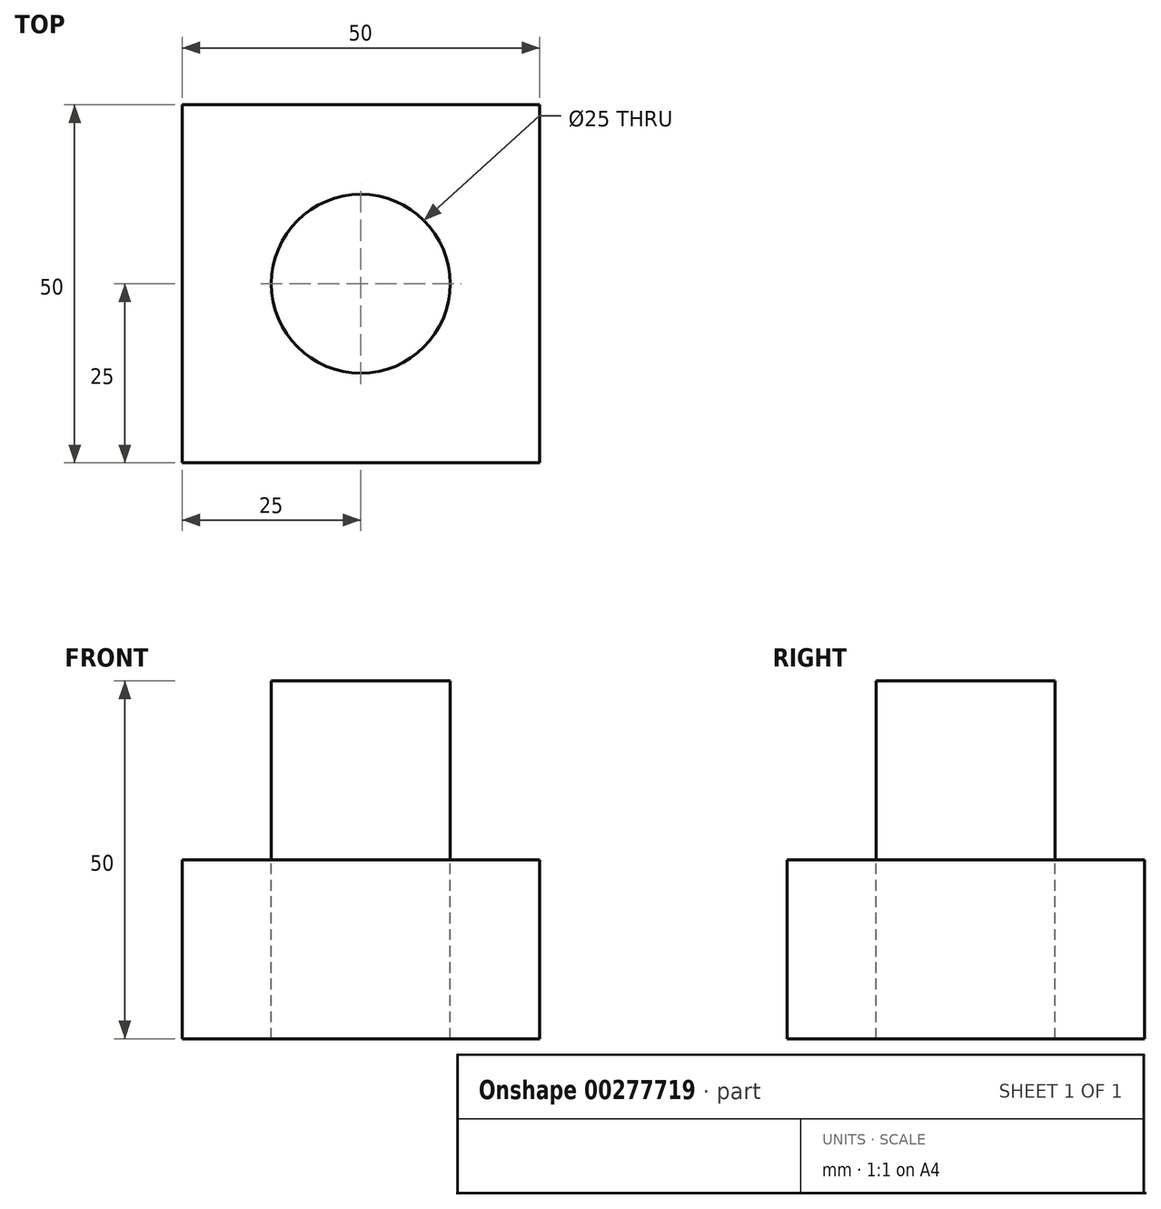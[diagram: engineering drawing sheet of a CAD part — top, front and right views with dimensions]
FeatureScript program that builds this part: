
annotation { "Feature Type Name" : "Feature", "Feature Type Description" : "" }
export const myFeature = defineFeature(function(context is Context, id is Id, definition is map)
    precondition{}
    {
        {
            var Q0;
            Q0=qCreatedBy(makeId("Top.planeOp"),FACE);
            var sketch = newSketch(context, id + "F0", { "sketchPlane" : qUnion([Q0])});
            skLineSegment(sketch, "E0.bottom", {"start": v(0, 0) * mm, "end": v(50, 0) * mm});
            skLineSegment(sketch, "E0.top", {"start": v(0, 50) * mm, "end": v(50, 50) * mm});
            skLineSegment(sketch, "E0.left", {"start": v(0, 0) * mm, "end": v(0, 50) * mm});
            skLineSegment(sketch, "E0.right", {"start": v(50, 0) * mm, "end": v(50, 50) * mm});
            skSolve(sketch);
        }
        {
            var Q0;
            Q0 = qSketchRegion(id + "F0", true);
            extrude(context, id + "F1", {"entities" : qUnion([Q0]), "depth" : 25 * mm});
        }
        {
            var Q0;
            Q0=makeQuery(id+"F1.opExtrude","CAP_FACE",FACE,{"disambiguationData":[OSD([sQuery(id+"F0.wireOp",EDGE,"E0.bottom"),sQuery(id+"F0.wireOp",EDGE,"E0.top"),sQuery(id+"F0.wireOp",EDGE,"E0.left"),sQuery(id+"F0.wireOp",EDGE,"E0.right")])],"isStart":false});
            var sketch = newSketch(context, id + "F2", { "sketchPlane" : qUnion([Q0])});
            skCircle(sketch, "E1", {"center": v(25, 25) * mm, "radius": 12.5 * mm});
            skPoint(sketch, "E1.centerSnap0", {"position": v(0, 25) * mm});
            skPoint(sketch, "E1.centerSnap1", {"position": v(25, 50) * mm});
            skSolve(sketch);
        }
        {
            var Q0;
            Q0 = qSketchRegion(id + "F2", true);
            extrude(context, id + "F3", {"entities" : qUnion([Q0]), "operationType" : NewBodyOperationType.REMOVE, "oppositeDirection" : true, "depth" : 25 * mm});
        }
        {
            var Q0;
            Q0=makeQuery(id+"F1.opExtrude","CAP_FACE",FACE,{"disambiguationData":[OSD([sQuery(id+"F0.wireOp",EDGE,"E0.bottom"),sQuery(id+"F0.wireOp",EDGE,"E0.top"),sQuery(id+"F0.wireOp",EDGE,"E0.left"),sQuery(id+"F0.wireOp",EDGE,"E0.right")])],"isStart":false});
            var sketch = newSketch(context, id + "F4", { "sketchPlane" : qUnion([Q0])});
            skCircle(sketch, "E2", {"center": v(25, 25) * mm, "radius": 12.5 * mm});
            skSolve(sketch);
        }
        {
            var Q0;
            Q0 = qSketchRegion(id + "F4", true);
            extrude(context, id + "F5", {"entities" : qUnion([Q0]), "depth" : 25 * mm});
        }
    });
